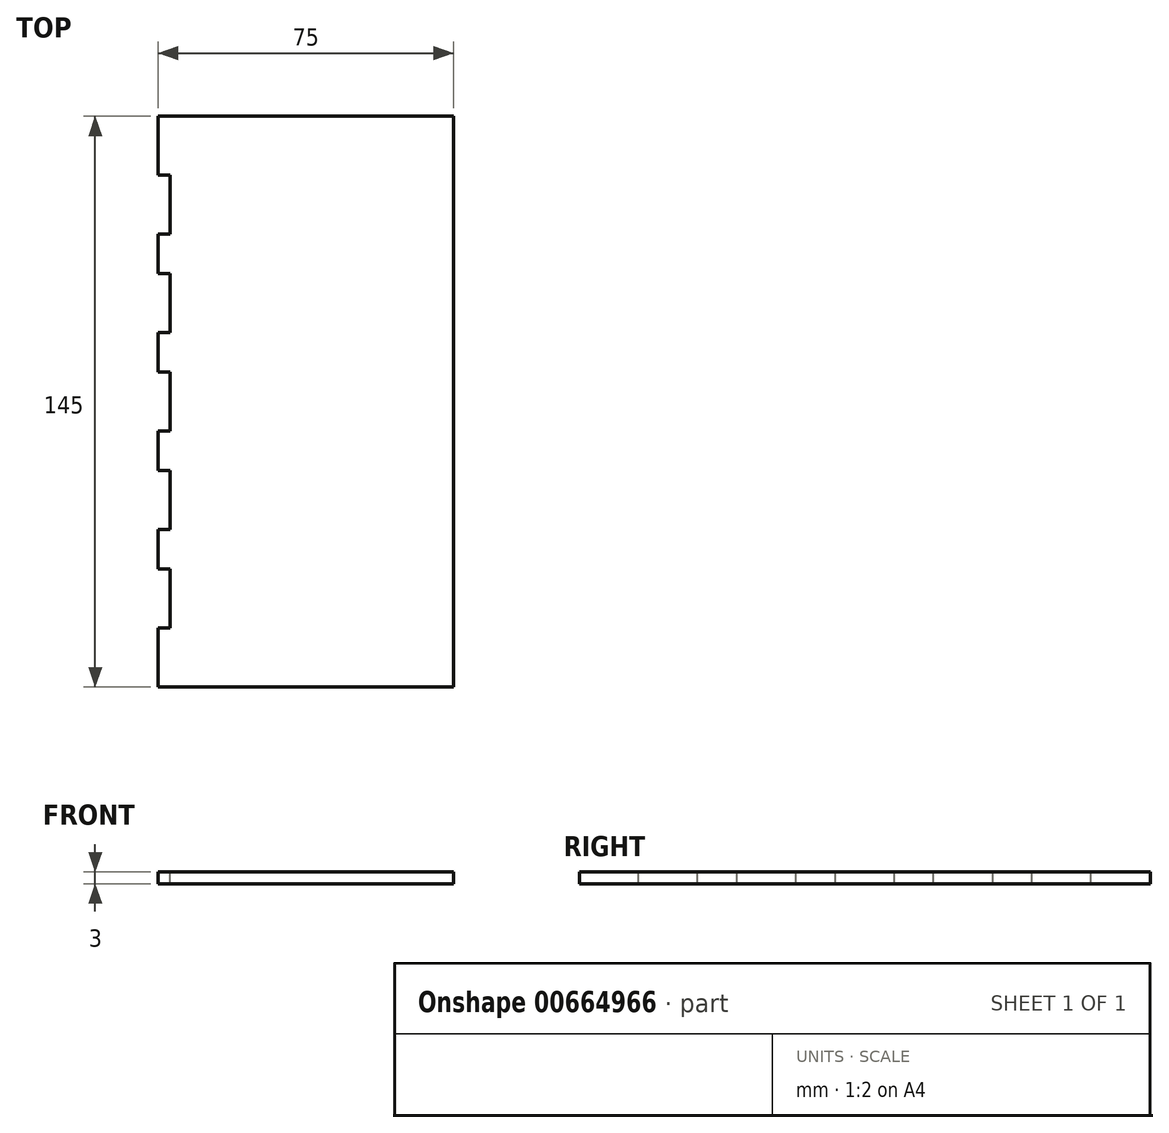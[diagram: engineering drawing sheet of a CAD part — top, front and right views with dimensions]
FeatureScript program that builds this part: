
annotation { "Feature Type Name" : "Feature", "Feature Type Description" : "" }
export const myFeature = defineFeature(function(context is Context, id is Id, definition is map)
    precondition{}
    {
        {
            var Q0;
            Q0=qCreatedBy(makeId("Right.planeOp"),FACE);
            var sketch = newSketch(context, id + "F0", { "sketchPlane" : qUnion([Q0])});
            skLineSegment(sketch, "E0.bottom", {"start": v(-32.27, 18.55) * mm, "end": v(113.95, 18.55) * mm});
            skLineSegment(sketch, "E0.top", {"start": v(-32.27, 13.9) * mm, "end": v(113.95, 13.9) * mm});
            skLineSegment(sketch, "E0.left", {"start": v(-32.27, 18.55) * mm, "end": v(-32.27, 13.9) * mm});
            skLineSegment(sketch, "E0.right", {"start": v(113.95, 18.55) * mm, "end": v(113.95, 13.9) * mm});
            skLineSegment(sketch, "E1.bottom", {"start": v(-32.27, 13.9) * mm, "end": v(-26.87, 13.9) * mm});
            skLineSegment(sketch, "E1.top", {"start": v(-32.27, -7.89) * mm, "end": v(-26.87, -7.89) * mm});
            skLineSegment(sketch, "E1.left", {"start": v(-32.27, 13.9) * mm, "end": v(-32.27, -7.89) * mm});
            skLineSegment(sketch, "E1.right", {"start": v(-26.87, 13.9) * mm, "end": v(-26.87, -7.89) * mm});
            skLineSegment(sketch, "E2.bottom", {"start": v(113.95, 13.9) * mm, "end": v(107.51, 13.9) * mm});
            skLineSegment(sketch, "E2.top", {"start": v(113.95, -47.04) * mm, "end": v(107.51, -47.04) * mm});
            skLineSegment(sketch, "E2.left", {"start": v(113.95, 13.9) * mm, "end": v(113.95, -47.04) * mm});
            skLineSegment(sketch, "E2.right", {"start": v(107.51, 13.9) * mm, "end": v(107.51, -47.04) * mm});
            skLineSegment(sketch, "E3", {"start": v(-32.27, 50.78) * mm, "end": v(113.95, 50.78) * mm, "construction": true});
            skSolve(sketch);
        }
        {
            var Q0;
            {var subQ0=sQuery(id+"F0.wireOp",EDGE,"E1.bottom");Q0=makeQuery(id+"F0.imprint","IMPRINT",FACE,{"disambiguationData":[TD([[makeQuery(id+"F0.imprint","IMPRINT",EDGE,{"derivedFrom":subQ0}),-1.0]])]});}
            var Q1;
            Q1=makeQuery(id+"F0.imprint","IMPRINT",FACE,{"disambiguationData":[TD([[makeQuery(id+"F0.imprint","IMPRINT",EDGE,{"derivedFrom":sQuery(id+"F0.wireOp",EDGE,"E0.bottom")}),-1.0]])]});
            var Q2;
            {var subQ0=sQuery(id+"F0.wireOp",EDGE,"E2.bottom");Q2=makeQuery(id+"F0.imprint","IMPRINT",FACE,{"disambiguationData":[TD([[makeQuery(id+"F0.imprint","IMPRINT",EDGE,{"derivedFrom":subQ0}),1.0]])]});}
            var Q3;
            {var subQ5=sQuery(id+"F0.wireOp",EDGE,"E1.top");Q3=makeQuery(id+"F0.imprint","IMPRINT",FACE,{"disambiguationData":[TD([[makeQuery(id+"F0.imprint","IMPRINT",EDGE,{"derivedFrom":subQ5}),-1.0]])]});}
            var Q4;
            {var subQ0=sQuery(id+"F0.wireOp",EDGE,"E2.top");Q4=makeQuery(id+"F0.imprint","IMPRINT",FACE,{"disambiguationData":[TD([[makeQuery(id+"F0.imprint","IMPRINT",EDGE,{"derivedFrom":subQ0}),-1.0]])]});}
            var Q5;
            {var subQ0=sQuery(id+"F0.wireOp",EDGE,"E1.top");Q5=makeQuery(id+"F0.imprint","IMPRINT",FACE,{"disambiguationData":[TD([[makeQuery(id+"F0.imprint","IMPRINT",EDGE,{"derivedFrom":subQ0}),1.0]])]});}
            extrude(context, id + "F1", {"entities" : qUnion([Q0, Q1, Q2, Q3, Q4, Q5]), "endBound" : BoundingType.SYMMETRIC, "depth" : 25 * mm, "offsetDistance" : 25 * mm});
        }
        {
            var Q0;
            Q0=makeQuery(id+"F1.opExtrude","SWEPT_FACE",FACE,{"disambiguationData":[OSD([sQuery(id+"F0.wireOp",EDGE,"E0.bottom")])]});
            var sketch = newSketch(context, id + "F2", { "sketchPlane" : qUnion([Q0])});
            skCircle(sketch, "E4", {"center": v(0, -28.05) * mm, "radius": 3 * mm});
            skCircle(sketch, "E5", {"center": v(0, -20.05) * mm, "radius": 3 * mm});
            skCircle(sketch, "E6", {"center": v(0, -12.05) * mm, "radius": 3.25 * mm});
            skCircle(sketch, "E7", {"center": v(0, -4.05) * mm, "radius": 3.25 * mm});
            skCircle(sketch, "E8", {"center": v(0, 3.95) * mm, "radius": 3.5 * mm});
            skCircle(sketch, "E9", {"center": v(0, 12.95) * mm, "radius": 3.5 * mm});
            skCircle(sketch, "E10", {"center": v(0, 21.95) * mm, "radius": 4 * mm});
            skCircle(sketch, "E11", {"center": v(0, 31.95) * mm, "radius": 4 * mm});
            skCircle(sketch, "E12", {"center": v(0, 41.95) * mm, "radius": 4.5 * mm});
            skCircle(sketch, "E13", {"center": v(0, 52.95) * mm, "radius": 4.5 * mm});
            skCircle(sketch, "E14", {"center": v(0, 64.95) * mm, "radius": 5 * mm});
            skCircle(sketch, "E15", {"center": v(0, 76.95) * mm, "radius": 5 * mm});
            skCircle(sketch, "E16", {"center": v(0, 89.95) * mm, "radius": 5.5 * mm});
            skCircle(sketch, "E17", {"center": v(0, 103.95) * mm, "radius": 5.5 * mm});
            skSolve(sketch);
        }
        {
            var Q0;
            Q0=makeQuery(id+"F1.opExtrude","SWEPT_FACE",FACE,{"disambiguationData":[OSD([sQuery(id+"F0.wireOp",EDGE,"E0.right"),sQuery(id+"F0.wireOp",EDGE,"E2.left")])]});
            var sketch = newSketch(context, id + "F3", { "sketchPlane" : qUnion([Q0])});
            skLineSegment(sketch, "E18.bottom", {"start": v(12.5, -47.04) * mm, "end": v(-12.5, -47.04) * mm});
            skLineSegment(sketch, "E18.top", {"start": v(12.5, 15.55) * mm, "end": v(-12.5, 15.55) * mm});
            skLineSegment(sketch, "E18.left", {"start": v(12.5, -47.04) * mm, "end": v(12.5, 15.55) * mm});
            skLineSegment(sketch, "E18.right", {"start": v(-12.5, -47.04) * mm, "end": v(-12.5, 15.55) * mm});
            skSolve(sketch);
        }
        {
            var Q0;
            Q0=qSketchRegion(id+"F3",true);
            var Q1;
            Q1=makeQuery(id+"F1.opExtrude","SWEPT_FACE",FACE,{"disambiguationData":[OSD([sQuery(id+"F0.wireOp",EDGE,"E0.left"),sQuery(id+"F0.wireOp",EDGE,"E1.left")])]});
            extrude(context, id + "F4", {"entities" : qUnion([Q0]), "operationType" : NewBodyOperationType.REMOVE, "endBound" : BoundingType.UP_TO_SURFACE, "oppositeDirection" : true, "depth" : 25 * mm, "endBoundEntityFace" : qUnion([Q1]), "offsetDistance" : 25 * mm});
        }
        {
            var Q0;
            Q0=makeQuery(id+"F1.opExtrude","CAP_FACE",FACE,{"disambiguationData":[OSD([sQuery(id+"F0.wireOp",EDGE,"E0.bottom"),sQuery(id+"F0.wireOp",EDGE,"E0.top"),sQuery(id+"F0.wireOp",EDGE,"E0.left"),sQuery(id+"F0.wireOp",EDGE,"E0.right"),sQuery(id+"F0.wireOp",EDGE,"E1.top"),sQuery(id+"F0.wireOp",EDGE,"E1.left"),sQuery(id+"F0.wireOp",EDGE,"E1.right"),sQuery(id+"F0.wireOp",EDGE,"E2.top"),sQuery(id+"F0.wireOp",EDGE,"E2.left"),sQuery(id+"F0.wireOp",EDGE,"E2.right")])],"isStart":true});
            extrude(context, id + "F5", {"entities" : qUnion([Q0]), "operationType" : NewBodyOperationType.ADD, "depth" : 25 * mm, "offsetDistance" : 25 * mm});
        }
        {
            var Q0;
            {var subQ0=sQuery(id+"F0.wireOp",EDGE,"E0.bottom");Q0=makeQuery(id+"F5.boolean.opBoolean","MERGE",FACE,{"derivedFrom":[makeQuery(id+"F1.opExtrude","SWEPT_FACE",FACE,{"disambiguationData":[OSD([subQ0])]}),makeQuery(id+"F5.opExtrude","SWEPT_FACE",FACE,{"disambiguationData":[OSD([subQ0])]})]});}
            var sketch = newSketch(context, id + "F6", { "sketchPlane" : qUnion([Q0])});
            skLineSegment(sketch, "E19.bottom", {"start": v(-37.5, -17.27) * mm, "end": v(-34.5, -17.27) * mm});
            skLineSegment(sketch, "E19.top", {"start": v(-37.5, -2.27) * mm, "end": v(-34.5, -2.27) * mm});
            skLineSegment(sketch, "E19.left", {"start": v(-37.5, -17.27) * mm, "end": v(-37.5, -2.27) * mm});
            skLineSegment(sketch, "E19.right", {"start": v(-34.5, -17.27) * mm, "end": v(-34.5, -2.27) * mm});
            skLineSegment(sketch, "E20.0.1.0", {"start": v(-37.5, 22.73) * mm, "end": v(-34.5, 22.73) * mm});
            skLineSegment(sketch, "E20.0.1.1", {"start": v(-37.5, 7.73) * mm, "end": v(-34.5, 7.73) * mm});
            skLineSegment(sketch, "E20.0.1.2", {"start": v(-37.5, 7.73) * mm, "end": v(-37.5, 22.73) * mm});
            skLineSegment(sketch, "E20.0.1.3", {"start": v(-34.5, 7.73) * mm, "end": v(-34.5, 22.73) * mm});
            skLineSegment(sketch, "E20.0.2.0", {"start": v(-37.5, 47.73) * mm, "end": v(-34.5, 47.73) * mm});
            skLineSegment(sketch, "E20.0.2.1", {"start": v(-37.5, 32.73) * mm, "end": v(-34.5, 32.73) * mm});
            skLineSegment(sketch, "E20.0.2.2", {"start": v(-37.5, 32.73) * mm, "end": v(-37.5, 47.73) * mm});
            skLineSegment(sketch, "E20.0.2.3", {"start": v(-34.5, 32.73) * mm, "end": v(-34.5, 47.73) * mm});
            skLineSegment(sketch, "E20.0.3.0", {"start": v(-37.5, 72.73) * mm, "end": v(-34.5, 72.73) * mm});
            skLineSegment(sketch, "E20.0.3.1", {"start": v(-37.5, 57.73) * mm, "end": v(-34.5, 57.73) * mm});
            skLineSegment(sketch, "E20.0.3.2", {"start": v(-37.5, 57.73) * mm, "end": v(-37.5, 72.73) * mm});
            skLineSegment(sketch, "E20.0.3.3", {"start": v(-34.5, 57.73) * mm, "end": v(-34.5, 72.73) * mm});
            skLineSegment(sketch, "E20.0.4.0", {"start": v(-37.5, 97.73) * mm, "end": v(-34.5, 97.73) * mm});
            skLineSegment(sketch, "E20.0.4.1", {"start": v(-37.5, 82.73) * mm, "end": v(-34.5, 82.73) * mm});
            skLineSegment(sketch, "E20.0.4.2", {"start": v(-37.5, 82.73) * mm, "end": v(-37.5, 97.73) * mm});
            skLineSegment(sketch, "E20.0.4.3", {"start": v(-34.5, 82.73) * mm, "end": v(-34.5, 97.73) * mm});
            skLineSegment(sketch, "E20.direction1", {"start": v(-37.5, -17.27) * mm, "end": v(-12.5, -17.27) * mm, "construction": true});
            skLineSegment(sketch, "E20.direction2", {"start": v(-37.5, -17.27) * mm, "end": v(-37.5, 7.73) * mm, "construction": true});
            skLineSegment(sketch, "E21.bottom", {"start": v(-37.5, 113.95) * mm, "end": v(12.5, 113.95) * mm});
            skLineSegment(sketch, "E21.top", {"start": v(-37.5, 112.73) * mm, "end": v(12.5, 112.73) * mm});
            skLineSegment(sketch, "E21.left", {"start": v(-37.5, 113.95) * mm, "end": v(-37.5, 112.73) * mm});
            skLineSegment(sketch, "E21.right", {"start": v(12.5, 113.95) * mm, "end": v(12.5, 112.73) * mm});
            skSolve(sketch);
        }
        {
            var Q0;
            Q0=qSketchRegion(id+"F6",true);
            extrude(context, id + "F7", {"entities" : qUnion([Q0]), "operationType" : NewBodyOperationType.REMOVE, "endBound" : BoundingType.UP_TO_NEXT, "oppositeDirection" : true, "depth" : 25 * mm, "offsetDistance" : 25 * mm});
        }
        {
            var Q0;
            Q0=makeQuery(id+"F1.opExtrude","CAP_FACE",FACE,{"disambiguationData":[OSD([sQuery(id+"F0.wireOp",EDGE,"E0.bottom"),sQuery(id+"F0.wireOp",EDGE,"E0.top"),sQuery(id+"F0.wireOp",EDGE,"E0.left"),sQuery(id+"F0.wireOp",EDGE,"E0.right"),sQuery(id+"F0.wireOp",EDGE,"E1.top"),sQuery(id+"F0.wireOp",EDGE,"E1.left"),sQuery(id+"F0.wireOp",EDGE,"E1.right"),sQuery(id+"F0.wireOp",EDGE,"E2.top"),sQuery(id+"F0.wireOp",EDGE,"E2.left"),sQuery(id+"F0.wireOp",EDGE,"E2.right")])],"isStart":false});
            extrude(context, id + "F8", {"entities" : qUnion([Q0]), "operationType" : NewBodyOperationType.ADD, "depth" : 25 * mm, "offsetDistance" : 25 * mm});
        }
    });
